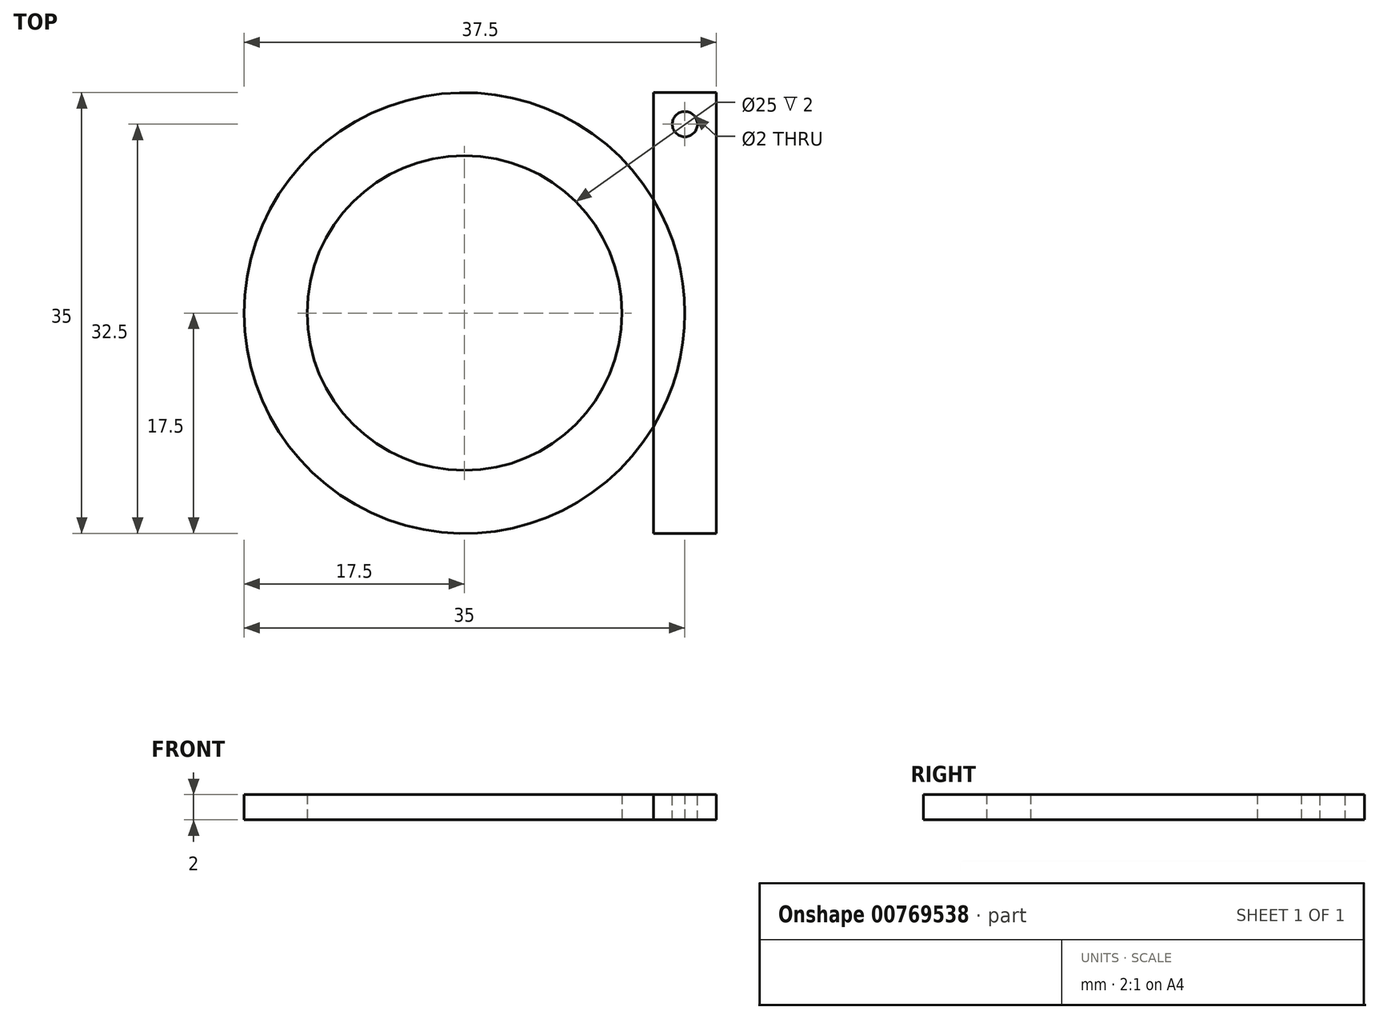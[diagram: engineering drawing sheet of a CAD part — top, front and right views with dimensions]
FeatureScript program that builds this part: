
annotation { "Feature Type Name" : "Feature", "Feature Type Description" : "" }
export const myFeature = defineFeature(function(context is Context, id is Id, definition is map)
    precondition{}
    {
        {
            var Q0;
            Q0=qCreatedBy(makeId("Top.planeOp"),FACE);
            var sketch = newSketch(context, id + "F0", { "sketchPlane" : qUnion([Q0])});
            skCircle(sketch, "E0", {"center": v(0, 0) * mm, "radius": 17.5 * mm});
            skCircle(sketch, "E1", {"center": v(0, 0) * mm, "radius": 12.5 * mm});
            skLineSegment(sketch, "E2.bottom", {"start": v(15, 17.5) * mm, "end": v(20, 17.5) * mm});
            skLineSegment(sketch, "E2.top", {"start": v(15, -17.5) * mm, "end": v(20, -17.5) * mm});
            skLineSegment(sketch, "E2.left", {"start": v(15, 17.5) * mm, "end": v(15, -17.5) * mm});
            skLineSegment(sketch, "E2.right", {"start": v(20, 17.5) * mm, "end": v(20, -17.5) * mm});
            skSolve(sketch);
        }
        {
            var Q0;
            Q0=makeQuery(id+"F0.imprint","IMPRINT",FACE,{"disambiguationData":[TD([[makeQuery(id+"F0.imprint","IMPRINT",EDGE,{"derivedFrom":sQuery(id+"F0.wireOp",EDGE,"E1")}),-1.0]])]});
            var Q1;
            {var subQ1=sQuery(id+"F0.wireOp",EDGE,"E2.bottom");Q1=makeQuery(id+"F0.imprint","IMPRINT",FACE,{"disambiguationData":[TD([[makeQuery(id+"F0.imprint","IMPRINT",EDGE,{"derivedFrom":subQ1}),-1.0]])]});}
            var Q2;
            {var subQ0=sQuery(id+"F0.wireOp",EDGE,"E2.left");var subQ1=sQuery(id+"F0.wireOp",EDGE,"E0");var subQ2=makeQuery(id+"F0.imprint","INTERSECT",VERTEX,{"disambiguationData":[OD(0.0)],"derivedFrom":[subQ1,subQ0]});Q2=makeQuery(id+"F0.imprint","IMPRINT",FACE,{"disambiguationData":[TD([[makeQuery(id+"F0.imprint","IMPRINT",EDGE,{"disambiguationData":[TD([[subQ2,1.0]])],"derivedFrom":subQ1}),1.0]])]});}
            extrude(context, id + "F1", {"entities" : qUnion([Q0, Q1, Q2]), "depth" : 2 * mm, "offsetDistance" : 25 * mm});
        }
        {
            var Q0;
            Q0=makeQuery(id+"F1.opExtrude","CAP_FACE",FACE,{"disambiguationData":[OSD([sQuery(id+"F0.wireOp",EDGE,"E0"),sQuery(id+"F0.wireOp",EDGE,"E1"),sQuery(id+"F0.wireOp",EDGE,"E2.bottom"),sQuery(id+"F0.wireOp",EDGE,"E2.top"),sQuery(id+"F0.wireOp",EDGE,"E2.left"),sQuery(id+"F0.wireOp",EDGE,"E2.right")])],"isStart":false});
            var sketch = newSketch(context, id + "F2", { "sketchPlane" : qUnion([Q0])});
            skCircle(sketch, "E3", {"center": v(17.5, 15) * mm, "radius": 1 * mm});
            skSolve(sketch);
        }
        {
            var Q0;
            Q0 = qSketchRegion(id + "F2", true);
            extrude(context, id + "F3", {"entities" : qUnion([Q0]), "operationType" : NewBodyOperationType.REMOVE, "oppositeDirection" : true, "depth" : 2 * mm, "offsetDistance" : 25 * mm});
        }
    });
